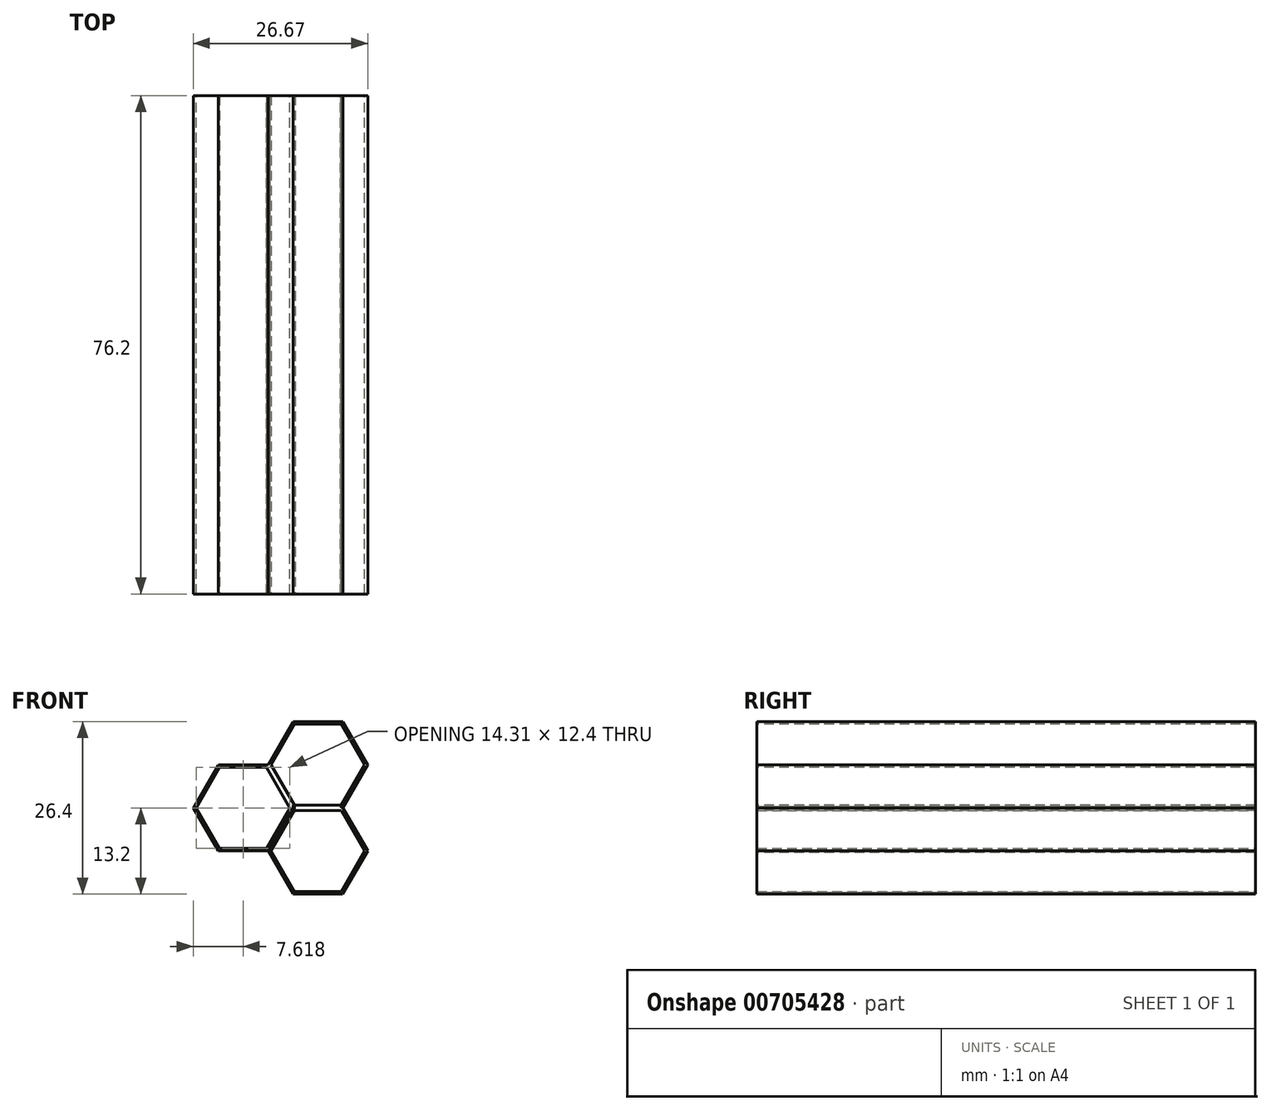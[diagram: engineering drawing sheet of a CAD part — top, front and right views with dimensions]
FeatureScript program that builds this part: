
annotation { "Feature Type Name" : "Feature", "Feature Type Description" : "" }
export const myFeature = defineFeature(function(context is Context, id is Id, definition is map)
    precondition{}
    {
        {
            var Q0;
            Q0=qCreatedBy(makeId("Front.planeOp"),FACE);
            var sketch = newSketch(context, id + "F0", { "sketchPlane" : qUnion([Q0])});
            skLineSegment(sketch, "E0", {"start": v(0, 0) * mm, "end": v(-7.62, 0) * mm});
            skLineSegment(sketch, "E1.MirrorCS", {"start": v(0, 0) * mm, "end": v(7.62, 0) * mm});
            skLineSegment(sketch, "E2.MirrorCS", {"start": v(-3.8, 6.6) * mm, "end": v(0, 6.6) * mm});
            skLineSegment(sketch, "E3", {"start": v(-7.62, 0) * mm, "end": v(-3.8, 6.6) * mm});
            skLineSegment(sketch, "E4", {"start": v(0, 6.6) * mm, "end": v(3.81, 6.6) * mm});
            skLineSegment(sketch, "E5", {"start": v(3.81, 6.6) * mm, "end": v(7.62, 0) * mm});
            skLineSegment(sketch, "E6.MirrorCS", {"start": v(-7.62, 0) * mm, "end": v(-3.8, -6.6) * mm});
            skLineSegment(sketch, "E7.MirrorCS", {"start": v(-3.8, -6.6) * mm, "end": v(0, -6.6) * mm});
            skLineSegment(sketch, "E8.MirrorCS", {"start": v(0, -6.6) * mm, "end": v(3.81, -6.6) * mm});
            skLineSegment(sketch, "E9.MirrorCS", {"start": v(3.81, -6.6) * mm, "end": v(7.62, 0) * mm});
            skLineSegment(sketch, "E10.MirrorCS", {"start": v(3.8, 6.6) * mm, "end": v(7.62, 0) * mm});
            skLineSegment(sketch, "E11.MirrorCS", {"start": v(-3.81, 6.6) * mm, "end": v(0, 6.6) * mm});
            skLineSegment(sketch, "E12.MirrorCS", {"start": v(0, 6.6) * mm, "end": v(3.8, 6.6) * mm});
            skLineSegment(sketch, "E13", {"start": v(11.43, 6.6) * mm, "end": v(3.8, 6.6) * mm});
            skLineSegment(sketch, "E14.MirrorCS", {"start": v(11.43, 6.6) * mm, "end": v(19.05, 6.6) * mm});
            skLineSegment(sketch, "E15.MirrorCS", {"start": v(7.62, 13.2) * mm, "end": v(11.43, 13.2) * mm});
            skLineSegment(sketch, "E16", {"start": v(3.8, 6.6) * mm, "end": v(7.62, 13.2) * mm});
            skLineSegment(sketch, "E17", {"start": v(11.43, 13.2) * mm, "end": v(15.24, 13.2) * mm});
            skLineSegment(sketch, "E18", {"start": v(15.24, 13.2) * mm, "end": v(19.05, 6.6) * mm});
            skLineSegment(sketch, "E19.MirrorCS", {"start": v(7.62, 0) * mm, "end": v(11.43, 0) * mm});
            skLineSegment(sketch, "E20.MirrorCS", {"start": v(11.43, 0) * mm, "end": v(15.24, 0) * mm});
            skLineSegment(sketch, "E21.MirrorCS", {"start": v(15.24, 0) * mm, "end": v(19.05, 6.6) * mm});
            skLineSegment(sketch, "E22.MirrorCS", {"start": v(3.81, 6.6) * mm, "end": v(7.62, 13.2) * mm});
            skLineSegment(sketch, "E23", {"start": v(11.42, -6.6) * mm, "end": v(3.8, -6.6) * mm});
            skLineSegment(sketch, "E24.MirrorCS", {"start": v(11.42, -6.6) * mm, "end": v(19.04, -6.6) * mm});
            skLineSegment(sketch, "E25.MirrorCS", {"start": v(7.61, 0) * mm, "end": v(11.42, 0) * mm});
            skLineSegment(sketch, "E26", {"start": v(11.42, 0) * mm, "end": v(15.23, 0) * mm});
            skLineSegment(sketch, "E27", {"start": v(15.23, 0) * mm, "end": v(19.04, -6.6) * mm});
            skLineSegment(sketch, "E28.MirrorCS", {"start": v(3.8, -6.6) * mm, "end": v(7.61, -13.2) * mm});
            skLineSegment(sketch, "E29.MirrorCS", {"start": v(7.61, -13.2) * mm, "end": v(11.42, -13.2) * mm});
            skLineSegment(sketch, "E30.MirrorCS", {"start": v(11.42, -13.2) * mm, "end": v(15.23, -13.2) * mm});
            skLineSegment(sketch, "E31.MirrorCS", {"start": v(15.23, -13.2) * mm, "end": v(19.04, -6.6) * mm});
            skLineSegment(sketch, "E32", {"start": v(15.23, -13.12) * mm, "end": v(19.04, -6.52) * mm});
            skLineSegment(sketch, "E33.MirrorCS", {"start": v(3.8, -6.6) * mm, "end": v(7.62, 0) * mm});
            skSolve(sketch);
        }
        {
            var Q0;
            Q0=sQuery(id+"F0.wireOp",EDGE,"E6.MirrorCS");
            var Q1;
            Q1=sQuery(id+"F0.wireOp",EDGE,"E2.MirrorCS");
            var Q2;
            Q2=sQuery(id+"F0.wireOp",EDGE,"E4");
            var Q3;
            Q3=sQuery(id+"F0.wireOp",EDGE,"E5");
            var Q4;
            Q4=sQuery(id+"F0.wireOp",EDGE,"E9.MirrorCS");
            var Q5;
            Q5=sQuery(id+"F0.wireOp",EDGE,"E8.MirrorCS");
            var Q6;
            Q6=sQuery(id+"F0.wireOp",EDGE,"E7.MirrorCS");
            var Q7;
            Q7=sQuery(id+"F0.wireOp",EDGE,"E3");
            extrude(context, id + "F1", {"bodyType" : ToolBodyType.SURFACE, "surfaceEntities" : qUnion([Q0, Q1, Q2, Q3, Q4, Q5, Q6, Q7]), "depth" : 76.2 * mm, "offsetDistance" : 25.4 * mm});
        }
        {
            var Q0;
            Q0=makeQuery(id+"F1.opExtrude","SWEPT_FACE",FACE,{"disambiguationData":[OSD([sQuery(id+"F0.wireOp",EDGE,"E2.MirrorCS"),sQuery(id+"F0.wireOp",EDGE,"E4")])]});
            extrude(context, id + "F2", {"entities" : qUnion([Q0]), "oppositeDirection" : true, "depth" : 0.4 * mm, "offsetDistance" : 25.4 * mm});
        }
        {
            var Q0;
            Q0=makeQuery(id+"F1.opExtrude","SWEPT_FACE",FACE,{"disambiguationData":[OSD([sQuery(id+"F0.wireOp",EDGE,"E9.MirrorCS")])]});
            extrude(context, id + "F3", {"entities" : qUnion([Q0]), "operationType" : NewBodyOperationType.ADD, "oppositeDirection" : true, "depth" : 0.4 * mm, "offsetDistance" : 25.4 * mm});
        }
        {
            var Q0;
            Q0=makeQuery(id+"F1.opExtrude","SWEPT_FACE",FACE,{"disambiguationData":[OSD([sQuery(id+"F0.wireOp",EDGE,"E7.MirrorCS"),sQuery(id+"F0.wireOp",EDGE,"E8.MirrorCS")])]});
            extrude(context, id + "F4", {"entities" : qUnion([Q0]), "operationType" : NewBodyOperationType.ADD, "oppositeDirection" : true, "depth" : 0.4 * mm, "offsetDistance" : 25.4 * mm});
        }
        {
            var Q0;
            Q0=makeQuery(id+"F1.opExtrude","SWEPT_FACE",FACE,{"disambiguationData":[OSD([sQuery(id+"F0.wireOp",EDGE,"E6.MirrorCS")])]});
            extrude(context, id + "F5", {"entities" : qUnion([Q0]), "operationType" : NewBodyOperationType.ADD, "oppositeDirection" : true, "depth" : 0.4 * mm, "offsetDistance" : 25.4 * mm});
        }
        {
            var Q0;
            Q0=makeQuery(id+"F1.opExtrude","SWEPT_FACE",FACE,{"disambiguationData":[OSD([sQuery(id+"F0.wireOp",EDGE,"E3")])]});
            extrude(context, id + "F6", {"entities" : qUnion([Q0]), "operationType" : NewBodyOperationType.ADD, "oppositeDirection" : true, "depth" : 0.4 * mm, "offsetDistance" : 25.4 * mm});
        }
        {
            var Q0;
            Q0=sQuery(id+"F0.wireOp",EDGE,"E25.MirrorCS");
            var Q1;
            Q1=sQuery(id+"F0.wireOp",EDGE,"E26");
            var Q2;
            Q2=sQuery(id+"F0.wireOp",EDGE,"E16");
            var Q3;
            Q3=sQuery(id+"F0.wireOp",EDGE,"E15.MirrorCS");
            var Q4;
            Q4=sQuery(id+"F0.wireOp",EDGE,"E17");
            var Q5;
            Q5=sQuery(id+"F0.wireOp",EDGE,"E18");
            var Q6;
            Q6=sQuery(id+"F0.wireOp",EDGE,"E21.MirrorCS");
            var Q7;
            Q7=sQuery(id+"F0.wireOp",EDGE,"E5");
            extrude(context, id + "F7", {"bodyType" : ToolBodyType.SURFACE, "surfaceEntities" : qUnion([Q0, Q1, Q2, Q3, Q4, Q5, Q6, Q7]), "depth" : 76.2 * mm, "offsetDistance" : 25.4 * mm});
        }
        {
            var Q0;
            Q0=sQuery(id+"F0.wireOp",EDGE,"E27");
            var Q1;
            Q1=sQuery(id+"F0.wireOp",EDGE,"E31.MirrorCS");
            var Q2;
            Q2=sQuery(id+"F0.wireOp",EDGE,"E30.MirrorCS");
            var Q3;
            Q3=sQuery(id+"F0.wireOp",EDGE,"E29.MirrorCS");
            var Q4;
            Q4=sQuery(id+"F0.wireOp",EDGE,"E28.MirrorCS");
            var Q5;
            Q5=sQuery(id+"F0.wireOp",EDGE,"E9.MirrorCS");
            extrude(context, id + "F8", {"bodyType" : ToolBodyType.SURFACE, "surfaceEntities" : qUnion([Q0, Q1, Q2, Q3, Q4, Q5]), "depth" : 76.2 * mm, "offsetDistance" : 25.4 * mm});
        }
        {
            var Q0;
            Q0=makeQuery(id+"F7.opExtrude","SWEPT_FACE",FACE,{"disambiguationData":[OSD([sQuery(id+"F0.wireOp",EDGE,"E5")])]});
            extrude(context, id + "F9", {"entities" : qUnion([Q0]), "depth" : 0.4 * mm, "offsetDistance" : 25.4 * mm});
        }
        {
            var Q0;
            Q0=makeQuery(id+"F1.opExtrude","SWEPT_FACE",FACE,{"disambiguationData":[OSD([sQuery(id+"F0.wireOp",EDGE,"E5")])]});
            extrude(context, id + "F10", {"entities" : qUnion([Q0]), "operationType" : NewBodyOperationType.ADD, "depth" : 0.4 * mm, "offsetDistance" : 25.4 * mm});
        }
        {
            var Q0;
            Q0=makeQuery(id+"F7.opExtrude","SWEPT_FACE",FACE,{"disambiguationData":[OSD([sQuery(id+"F0.wireOp",EDGE,"E16")])]});
            extrude(context, id + "F11", {"entities" : qUnion([Q0]), "operationType" : NewBodyOperationType.ADD, "oppositeDirection" : true, "depth" : 0.4 * mm, "offsetDistance" : 25.4 * mm});
        }
        {
            var Q0;
            Q0=makeQuery(id+"F7.opExtrude","SWEPT_FACE",FACE,{"disambiguationData":[OSD([sQuery(id+"F0.wireOp",EDGE,"E17"),sQuery(id+"F0.wireOp",EDGE,"E15.MirrorCS")])]});
            extrude(context, id + "F12", {"entities" : qUnion([Q0]), "oppositeDirection" : true, "depth" : 0.4 * mm, "offsetDistance" : 25.4 * mm});
        }
        {
            var Q0;
            Q0=makeQuery(id+"F7.opExtrude","SWEPT_FACE",FACE,{"disambiguationData":[OSD([sQuery(id+"F0.wireOp",EDGE,"E18")])]});
            extrude(context, id + "F13", {"entities" : qUnion([Q0]), "oppositeDirection" : true, "depth" : 0.4 * mm, "offsetDistance" : 25.4 * mm});
        }
        {
            var Q0;
            Q0=makeQuery(id+"F7.opExtrude","SWEPT_FACE",FACE,{"disambiguationData":[OSD([sQuery(id+"F0.wireOp",EDGE,"E21.MirrorCS")])]});
            extrude(context, id + "F14", {"entities" : qUnion([Q0]), "operationType" : NewBodyOperationType.ADD, "oppositeDirection" : true, "depth" : 0.4 * mm, "offsetDistance" : 25.4 * mm});
        }
        {
            var Q0;
            Q0=makeQuery(id+"F7.opExtrude","SWEPT_FACE",FACE,{"disambiguationData":[OSD([sQuery(id+"F0.wireOp",EDGE,"E25.MirrorCS"),sQuery(id+"F0.wireOp",EDGE,"E26")])]});
            extrude(context, id + "F15", {"entities" : qUnion([Q0]), "oppositeDirection" : true, "depth" : 0.4 * mm, "offsetDistance" : 25.4 * mm});
        }
        {
            var Q0;
            Q0=makeQuery(id+"F7.opExtrude","SWEPT_FACE",FACE,{"disambiguationData":[OSD([sQuery(id+"F0.wireOp",EDGE,"E25.MirrorCS"),sQuery(id+"F0.wireOp",EDGE,"E26")])]});
            extrude(context, id + "F16", {"entities" : qUnion([Q0]), "depth" : 0.4 * mm, "offsetDistance" : 25.4 * mm});
        }
        {
            var Q0;
            Q0=makeQuery(id+"F8.opExtrude","SWEPT_FACE",FACE,{"disambiguationData":[OSD([sQuery(id+"F0.wireOp",EDGE,"E27")])]});
            extrude(context, id + "F17", {"entities" : qUnion([Q0]), "operationType" : NewBodyOperationType.ADD, "depth" : 0.4 * mm, "offsetDistance" : 25.4 * mm});
        }
        {
            var Q0;
            Q0=makeQuery(id+"F8.opExtrude","SWEPT_FACE",FACE,{"disambiguationData":[OSD([sQuery(id+"F0.wireOp",EDGE,"E31.MirrorCS")])]});
            extrude(context, id + "F18", {"entities" : qUnion([Q0]), "operationType" : NewBodyOperationType.ADD, "depth" : 0.4 * mm, "offsetDistance" : 25.4 * mm});
        }
        {
            var Q0;
            Q0=makeQuery(id+"F8.opExtrude","SWEPT_FACE",FACE,{"disambiguationData":[OSD([sQuery(id+"F0.wireOp",EDGE,"E29.MirrorCS"),sQuery(id+"F0.wireOp",EDGE,"E30.MirrorCS")])]});
            extrude(context, id + "F19", {"entities" : qUnion([Q0]), "operationType" : NewBodyOperationType.ADD, "depth" : 0.4 * mm, "offsetDistance" : 25.4 * mm});
        }
        {
            var Q0;
            Q0=makeQuery(id+"F8.opExtrude","SWEPT_FACE",FACE,{"disambiguationData":[OSD([sQuery(id+"F0.wireOp",EDGE,"E28.MirrorCS")])]});
            extrude(context, id + "F20", {"entities" : qUnion([Q0]), "depth" : 0.4 * mm, "offsetDistance" : 25.4 * mm});
        }
        {
            var Q0;
            Q0=makeQuery(id+"F1.opExtrude","SWEPT_FACE",FACE,{"disambiguationData":[OSD([sQuery(id+"F0.wireOp",EDGE,"E9.MirrorCS")])]});
            extrude(context, id + "F21", {"entities" : qUnion([Q0]), "depth" : 0.4 * mm, "offsetDistance" : 25.4 * mm});
        }
    });
